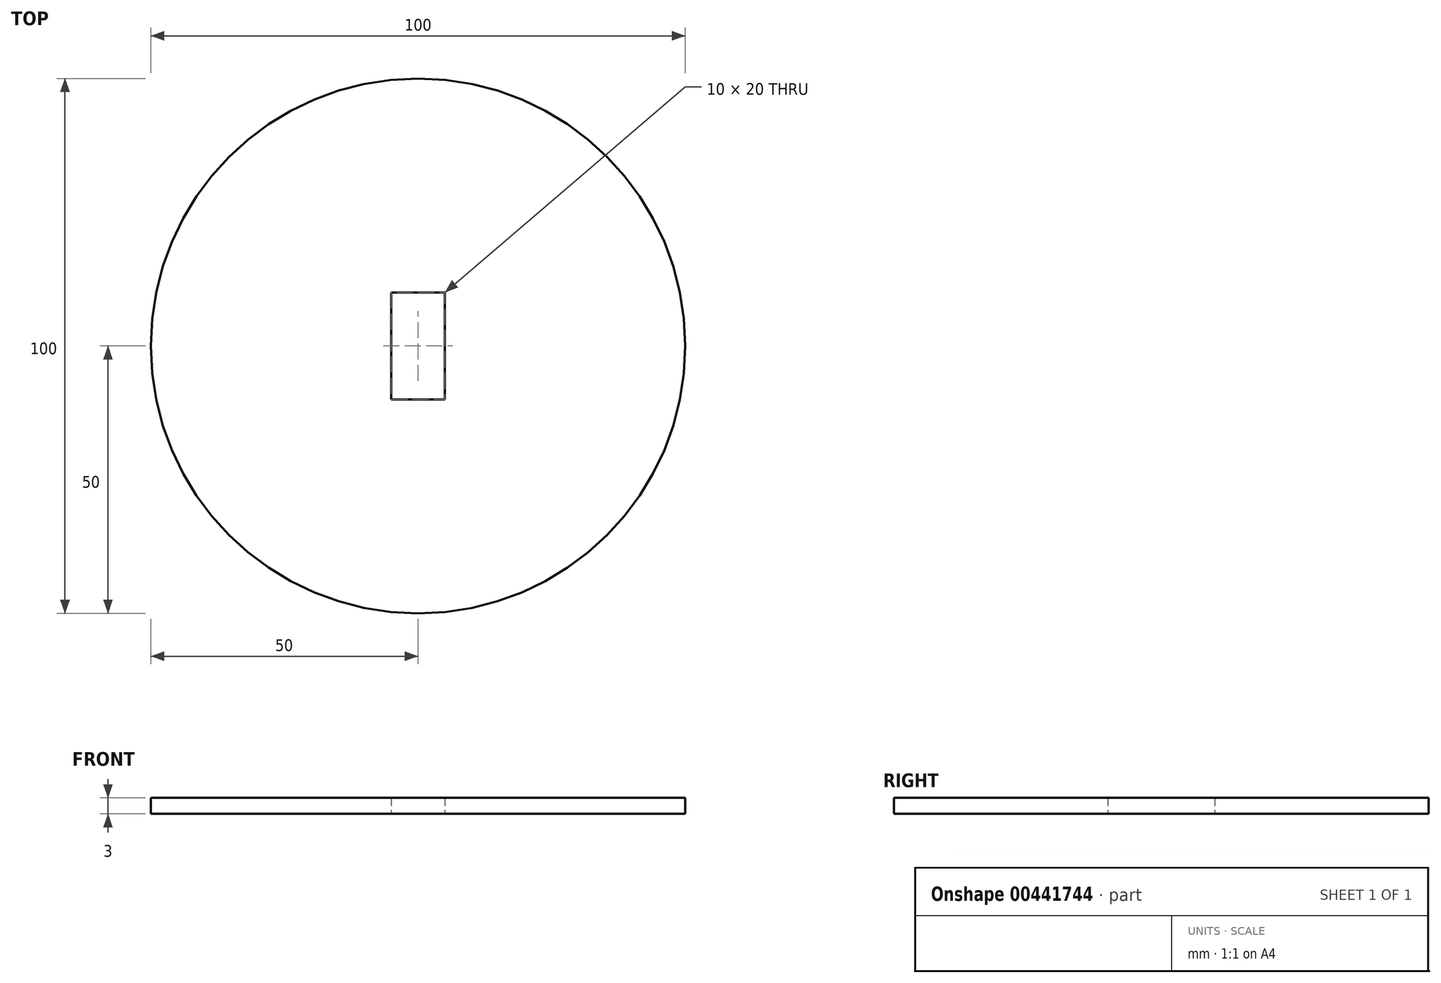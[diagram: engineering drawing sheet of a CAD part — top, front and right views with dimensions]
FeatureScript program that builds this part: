
annotation { "Feature Type Name" : "Feature", "Feature Type Description" : "" }
export const myFeature = defineFeature(function(context is Context, id is Id, definition is map)
    precondition{}
    {
        {
            var Q0;
            Q0=qCreatedBy(makeId("Top.planeOp"),FACE);
            var sketch = newSketch(context, id + "F0", { "sketchPlane" : qUnion([Q0])});
            skCircle(sketch, "E0", {"center": v(0, 0) * mm, "radius": 50 * mm});
            skLineSegment(sketch, "E1.bottom", {"start": v(-5, 10) * mm, "end": v(5, 10) * mm});
            skLineSegment(sketch, "E1.top", {"start": v(-5, -10) * mm, "end": v(5, -10) * mm});
            skLineSegment(sketch, "E1.left", {"start": v(-5, 10) * mm, "end": v(-5, -10) * mm});
            skLineSegment(sketch, "E1.right", {"start": v(5, 10) * mm, "end": v(5, -10) * mm});
            skSolve(sketch);
        }
        {
            var Q0;
            Q0 = qSketchRegion(id + "F0", true);
            extrude(context, id + "F1", {"entities" : qUnion([Q0]), "depth" : 3 * mm});
        }
    });
